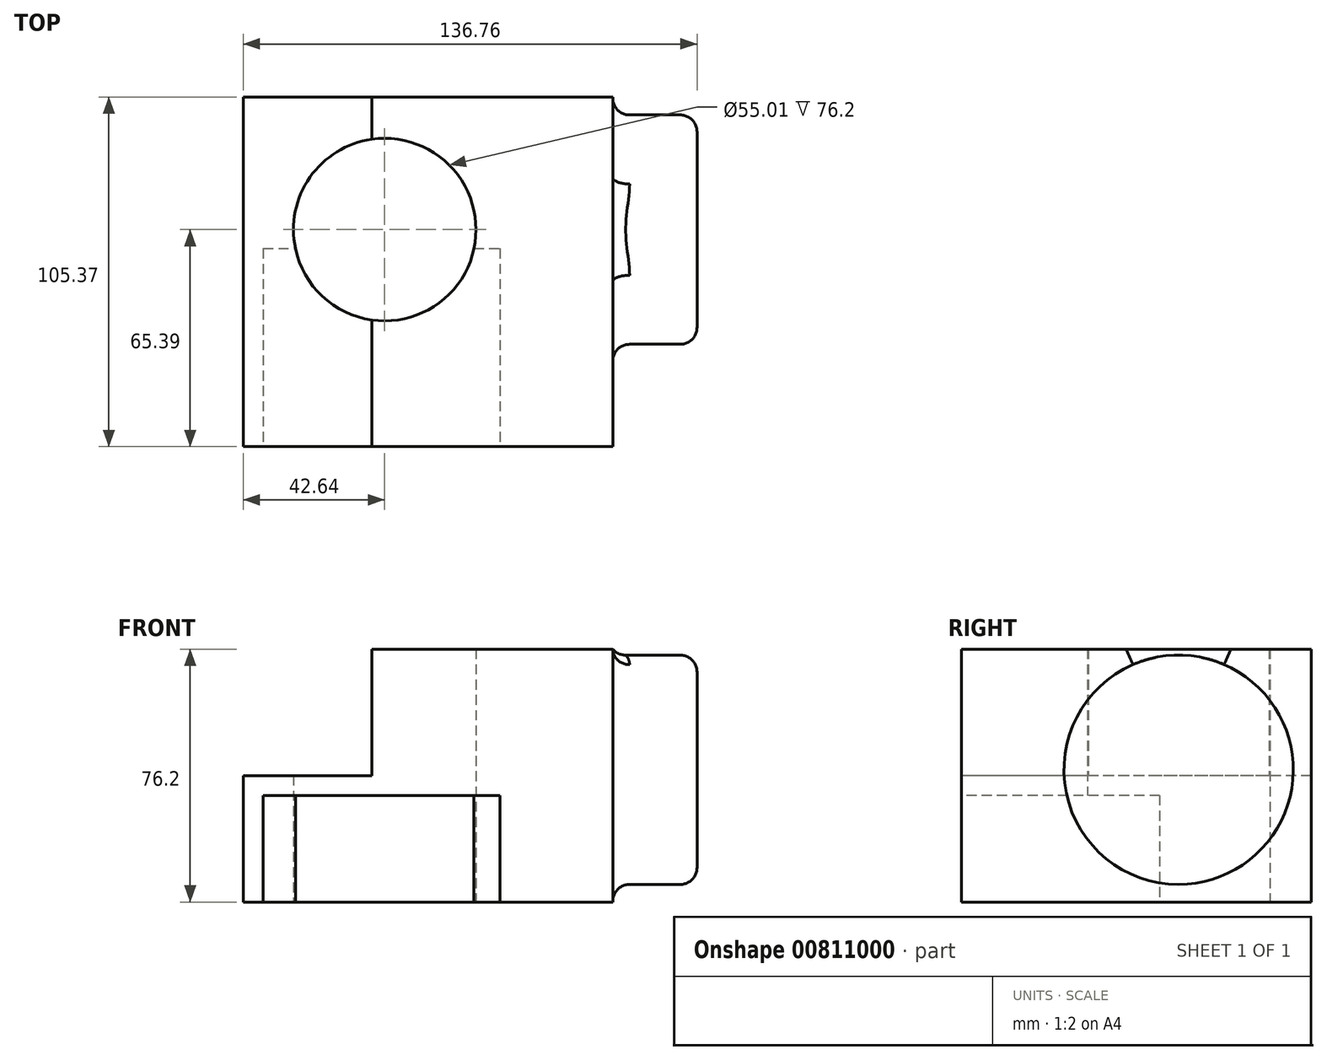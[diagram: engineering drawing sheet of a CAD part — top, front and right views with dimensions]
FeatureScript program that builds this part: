
annotation { "Feature Type Name" : "Feature", "Feature Type Description" : "" }
export const myFeature = defineFeature(function(context is Context, id is Id, definition is map)
    precondition{}
    {
        {
            var Q0;
            Q0=qCreatedBy(makeId("Top.planeOp"),FACE);
            var sketch = newSketch(context, id + "F0", { "sketchPlane" : qUnion([Q0])});
            skCircle(sketch, "E0", {"center": v(0, 0) * mm, "radius": 27.5 * mm});
            skSolve(sketch);
        }
        {
            var Q0;
            Q0=makeQuery(id+"F0.imprint","IMPRINT",FACE,{"disambiguationData":[TD([[makeQuery(id+"F0.imprint","IMPRINT",EDGE,{"derivedFrom":sQuery(id+"F0.wireOp",EDGE,"E0")}),1.0]])]});
            var sketch = newSketch(context, id + "F1", { "sketchPlane" : qUnion([Q0])});
            skLineSegment(sketch, "E1.bottom", {"start": v(-42.64, 39.98) * mm, "end": v(68.72, 39.98) * mm});
            skLineSegment(sketch, "E1.top", {"start": v(-42.64, -40) * mm, "end": v(68.72, -40) * mm});
            skLineSegment(sketch, "E1.left", {"start": v(-42.64, 39.98) * mm, "end": v(-42.64, -40) * mm});
            skLineSegment(sketch, "E1.right", {"start": v(68.72, 39.98) * mm, "end": v(68.72, -40) * mm});
            skSolve(sketch);
        }
        {
            var Q0;
            Q0=makeQuery(id+"F1.imprint","IMPRINT",FACE,{"disambiguationData":[TD([[makeQuery(id+"F1.imprint","IMPRINT",EDGE,{"derivedFrom":sQuery(id+"F1.wireOp",EDGE,"E1.bottom")}),-1.0]])]});
            extrude(context, id + "F2", {"entities" : qUnion([Q0]), "depth" : 38.1 * mm, "offsetDistance" : 25.4 * mm});
        }
        {
            var Q0;
            Q0=makeQuery(id+"F2.opExtrude","CAP_FACE",FACE,{"disambiguationData":[OSD([sQuery(id+"F0.wireOp",EDGE,"E0"),sQuery(id+"F1.wireOp",EDGE,"E1.bottom"),sQuery(id+"F1.wireOp",EDGE,"E1.top"),sQuery(id+"F1.wireOp",EDGE,"E1.left"),sQuery(id+"F1.wireOp",EDGE,"E1.right")])],"isStart":false});
            var sketch = newSketch(context, id + "F3", { "sketchPlane" : qUnion([Q0])});
            skLineSegment(sketch, "E2.bottom", {"start": v(-3.93, 39.98) * mm, "end": v(68.72, 39.98) * mm});
            skLineSegment(sketch, "E2.top", {"start": v(-3.93, -40) * mm, "end": v(68.72, -40) * mm});
            skLineSegment(sketch, "E2.left", {"start": v(-3.93, 39.98) * mm, "end": v(-3.93, -40) * mm});
            skLineSegment(sketch, "E2.right", {"start": v(68.72, 39.98) * mm, "end": v(68.72, -40) * mm});
            skSolve(sketch);
        }
        {
            var Q0;
            {var subQ4=sQuery(id+"F3.wireOp",EDGE,"E2.bottom");Q0=makeQuery(id+"F3.imprint","IMPRINT",FACE,{"disambiguationData":[TD([[makeQuery(id+"F3.imprint","IMPRINT",EDGE,{"derivedFrom":subQ4}),-1.0]])]});}
            extrude(context, id + "F4", {"entities" : qUnion([Q0]), "operationType" : NewBodyOperationType.ADD, "depth" : 38.1 * mm, "offsetDistance" : 25.4 * mm});
        }
        {
            var Q0;
            Q0=makeQuery(id+"F4.boolean.opBoolean","MERGE",FACE,{"derivedFrom":[makeQuery(id+"F2.opExtrude","SWEPT_FACE",FACE,{"disambiguationData":[OSD([sQuery(id+"F1.wireOp",EDGE,"E1.top")])]}),makeQuery(id+"F4.opExtrude","SWEPT_FACE",FACE,{"disambiguationData":[OSD([sQuery(id+"F3.wireOp",EDGE,"E2.top")])]})]});
            extrude(context, id + "F5", {"entities" : qUnion([Q0]), "operationType" : NewBodyOperationType.ADD, "depth" : 25.4 * mm, "offsetDistance" : 25.4 * mm});
        }
        {
            var Q0;
            Q0=makeQuery(id+"F5.opExtrude","CAP_FACE",FACE,{"disambiguationData":[OSD([sQuery(id+"F1.wireOp",EDGE,"E1.top"),sQuery(id+"F3.wireOp",EDGE,"E2.top")])],"isStart":false});
            var sketch = newSketch(context, id + "F6", { "sketchPlane" : qUnion([Q0])});
            skLineSegment(sketch, "E3.bottom", {"start": v(-36.58, 32.1) * mm, "end": v(34.68, 32.1) * mm});
            skLineSegment(sketch, "E3.top", {"start": v(-36.58, 0) * mm, "end": v(34.68, 0) * mm});
            skLineSegment(sketch, "E3.left", {"start": v(-36.58, 32.1) * mm, "end": v(-36.58, 0) * mm});
            skLineSegment(sketch, "E3.right", {"start": v(34.68, 32.1) * mm, "end": v(34.68, 0) * mm});
            skSolve(sketch);
        }
        {
            var Q0;
            Q0=makeQuery(id+"F6.imprint","IMPRINT",FACE,{"disambiguationData":[TD([[makeQuery(id+"F6.imprint","IMPRINT",EDGE,{"derivedFrom":sQuery(id+"F6.wireOp",EDGE,"E3.bottom")}),-1.0]])]});
            extrude(context, id + "F7", {"entities" : qUnion([Q0]), "operationType" : NewBodyOperationType.REMOVE, "oppositeDirection" : true, "depth" : 59.69 * mm, "offsetDistance" : 25.4 * mm});
        }
        {
            var Q0;
            {var subQ0=sQuery(id+"F3.wireOp",EDGE,"E2.right");var subQ1=sQuery(id+"F1.wireOp",EDGE,"E1.right");Q0=makeQuery(id+"F5.boolean.opBoolean","MERGE",FACE,{"derivedFrom":[makeQuery(id+"F4.boolean.opBoolean","MERGE",FACE,{"derivedFrom":[makeQuery(id+"F2.opExtrude","SWEPT_FACE",FACE,{"disambiguationData":[OSD([subQ1])]}),makeQuery(id+"F4.opExtrude","SWEPT_FACE",FACE,{"disambiguationData":[OSD([subQ0])]})]}),makeQuery(id+"F5.opExtrude","SWEPT_FACE",FACE,{"disambiguationData":[OSD([sQuery(id+"F1.wireOp",EDGE,"E1.top"),subQ1,sQuery(id+"F3.wireOp",EDGE,"E2.top"),subQ0])]})]});}
            var sketch = newSketch(context, id + "F8", { "sketchPlane" : qUnion([Q0])});
            skCircle(sketch, "E4", {"center": v(0, 39.84) * mm, "radius": 34.55 * mm});
            skSolve(sketch);
        }
        {
            var Q0;
            Q0=makeQuery(id+"F8.imprint","IMPRINT",FACE,{"disambiguationData":[TD([[makeQuery(id+"F8.imprint","IMPRINT",EDGE,{"derivedFrom":sQuery(id+"F8.wireOp",EDGE,"E4")}),1.0]])]});
            extrude(context, id + "F9", {"entities" : qUnion([Q0]), "operationType" : NewBodyOperationType.ADD, "depth" : 25.4 * mm, "offsetDistance" : 25.4 * mm});
        }
        {
            var Q0;
            Q0=makeQuery(id+"F9.opExtrude","SWEPT_FACE",FACE,{"disambiguationData":[OSD([sQuery(id+"F8.wireOp",EDGE,"E4")])]});
            fillet(context, id + "F10", {"entities" : qUnion([Q0]), "radius" : 5.08 * mm, "tangentPropagation" : true, "allowEdgeOverflow" : false});
        }
    });
